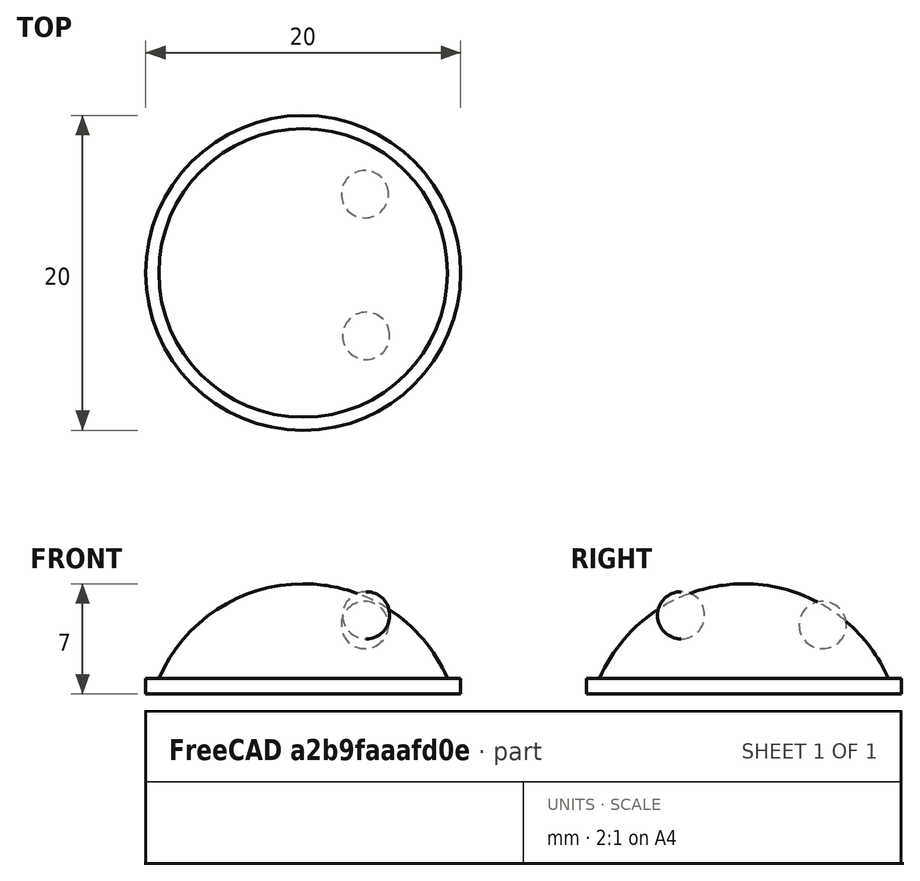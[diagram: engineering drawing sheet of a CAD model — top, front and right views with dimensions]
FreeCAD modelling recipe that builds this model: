
FCSTD DOCUMENT  (FreeCAD 1.0R39285 (Git))
Label: ojt1_t13r01_robot
License: All rights reserved
objects: Part::Sphere×3, Part::Cylinder×1, Part::MultiFuse×1
note: 5 computed .brp shape members not serialized (recipe doc carries the construction recipe); baked Part::Feature solids carry a one-line shape summary decoded from their .brp

FEATURE [Part::Cylinder] Cylinder  label="basis"
  Angle = 360
  AttacherType = Attacher::AttachEngine3D
  FirstAngle = 0
  Height = 1
  Radius = 10
  SecondAngle = 0
FEATURE [Part::Sphere] Sphere  label="head"
  Angle1 = 20
  Angle2 = 90
  Angle3 = 360
  AttacherType = Attacher::AttachEngine3D
  Placement = pos=(0,0,-3) rot=(0,0,1;0rad)
  Radius = 10
FEATURE [Part::Sphere] Sphere001  label="eye1"
  Angle1 = -90
  Angle2 = 90
  Angle3 = 360
  AttacherType = Attacher::AttachEngine3D
  Placement = pos=(4,-4,5) rot=(0,0,1;0rad)
  Radius = 1.5
FEATURE [Part::Sphere] Sphere002  label="eye2"
  Angle1 = -90
  Angle2 = 90
  Angle3 = 360
  AttacherType = Attacher::AttachEngine3D
  Placement = pos=(3.92388,5,4.38268) rot=(0,1,0;5.89049rad)
  Radius = 1.5
FEATURE [Part::MultiFuse] Fusion
  Refine = true
  Shapes = -> [Cylinder,Sphere]
